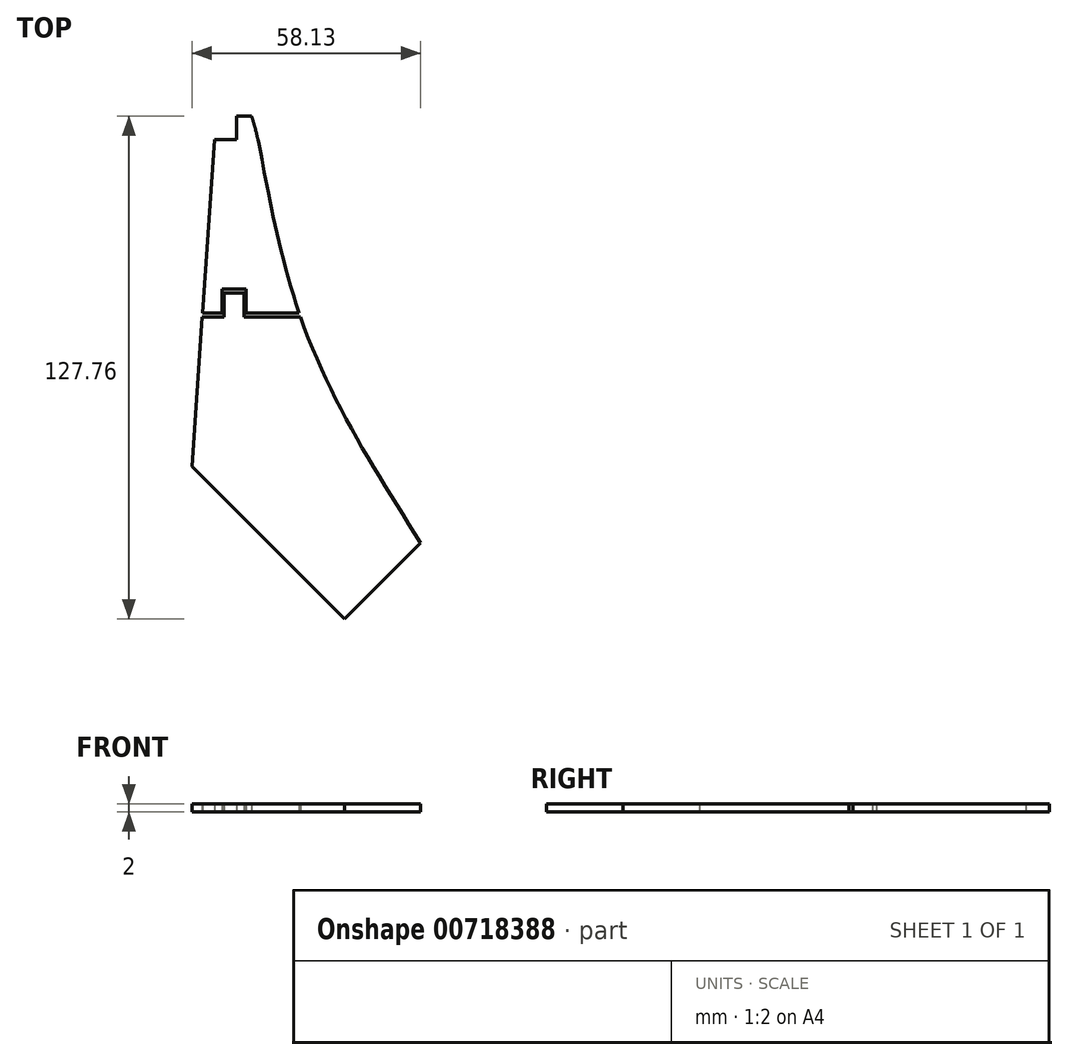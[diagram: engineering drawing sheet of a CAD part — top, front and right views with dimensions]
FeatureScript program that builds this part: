
annotation { "Feature Type Name" : "Feature", "Feature Type Description" : "" }
export const myFeature = defineFeature(function(context is Context, id is Id, definition is map)
    precondition{}
    {
        {
            var Q0;
            Q0=qCreatedBy(makeId("Top.planeOp"),FACE);
            var sketch = newSketch(context, id + "F0", { "sketchPlane" : qUnion([Q0])});
            skLineSegment(sketch, "E0", {"start": v(-38.75, -56.1) * mm, "end": v(0.02, -94.87) * mm});
            skLineSegment(sketch, "E1", {"start": v(0.02, -94.87) * mm, "end": v(19.38, -75.51) * mm});
            skLineSegment(sketch, "E2.left", {"start": v(-31.03, -17.1) * mm, "end": v(-31.03, -11.1) * mm});
            skLineSegment(sketch, "E2.right", {"start": v(-25.03, -17.1) * mm, "end": v(-25.03, -11.1) * mm});
            skLineSegment(sketch, "E3", {"start": v(-36.03, -17.1) * mm, "end": v(-31.03, -17.1) * mm});
            skLineSegment(sketch, "E4", {"start": v(-31.03, -11.1) * mm, "end": v(-25.03, -11.1) * mm});
            skLineSegment(sketch, "E5", {"start": v(-32.97, 26.9) * mm, "end": v(-27.4, 26.9) * mm});
            skLineSegment(sketch, "E6", {"start": v(-36.1, -18.1) * mm, "end": v(-30.53, -18.1) * mm});
            skLineSegment(sketch, "E7.top", {"start": v(-27.4, 32.9) * mm, "end": v(-23.58, 32.9) * mm});
            skLineSegment(sketch, "E7.left", {"start": v(-27.4, 26.9) * mm, "end": v(-27.4, 32.9) * mm});
            skLineSegment(sketch, "E7.right", {"start": v(-22.4, 26.9) * mm, "end": v(-22.4, 28.78) * mm});
            skLineSegment(sketch, "E8.top", {"start": v(-30.53, -12.1) * mm, "end": v(-25.53, -12.1) * mm});
            skLineSegment(sketch, "E8.left", {"start": v(-30.53, -18.1) * mm, "end": v(-30.53, -12.1) * mm});
            skLineSegment(sketch, "E8.right", {"start": v(-25.53, -18.1) * mm, "end": v(-25.53, -12.1) * mm});
            skLineSegment(sketch, "E9.trimOffspring", {"start": v(-32.97, 26.9) * mm, "end": v(-36.03, -17.1) * mm});
            skLineSegment(sketch, "E10.trimOffspring", {"start": v(-22.4, 26.9) * mm, "end": v(-21.97, 26.9) * mm});
            skLineSegment(sketch, "E11.trimOffspring", {"start": v(-36.1, -18.1) * mm, "end": v(-38.75, -56.1) * mm});
            skLineSegment(sketch, "E12.trimOffspring", {"start": v(-25.03, -17.1) * mm, "end": v(-11.5, -17.1) * mm});
            skLineSegment(sketch, "E13", {"start": v(-11.16, -18.1) * mm, "end": v(-25.53, -18.1) * mm});
            skLineSegment(sketch, "E14", {"start": v(-32.97, 26.9) * mm, "end": v(-21.97, 26.9) * mm});
            skLineSegment(sketch, "E15", {"start": v(-33.41, 20.6) * mm, "end": v(-32.37, 35.55) * mm, "construction": true});
            skLineSegment(sketch, "E16", {"start": v(-32.56, 32.9) * mm, "end": v(-23.58, 32.9) * mm});
            skFitSpline(sketch, "E17", {"points": [v(-23.58, 32.9) * mm, v(-21.97, 26.9) * mm, v(-11.16, -18.1) * mm, v(19.38, -75.51) * mm], "startDerivative": vector(10.08, -31.4) * mm, "endDerivative": vector(75.27, -118.25) * mm});
            skPoint(sketch, "E18.orphan", {"position": v(-22.4, 32.9) * mm});
            skSolve(sketch);
        }
        {
            var Q0;
            Q0 = qSketchRegion(id + "F0", true);
            extrude(context, id + "F1", {"entities" : qUnion([Q0]), "depth" : 2 * mm, "offsetDistance" : 25 * mm});
        }
    });
